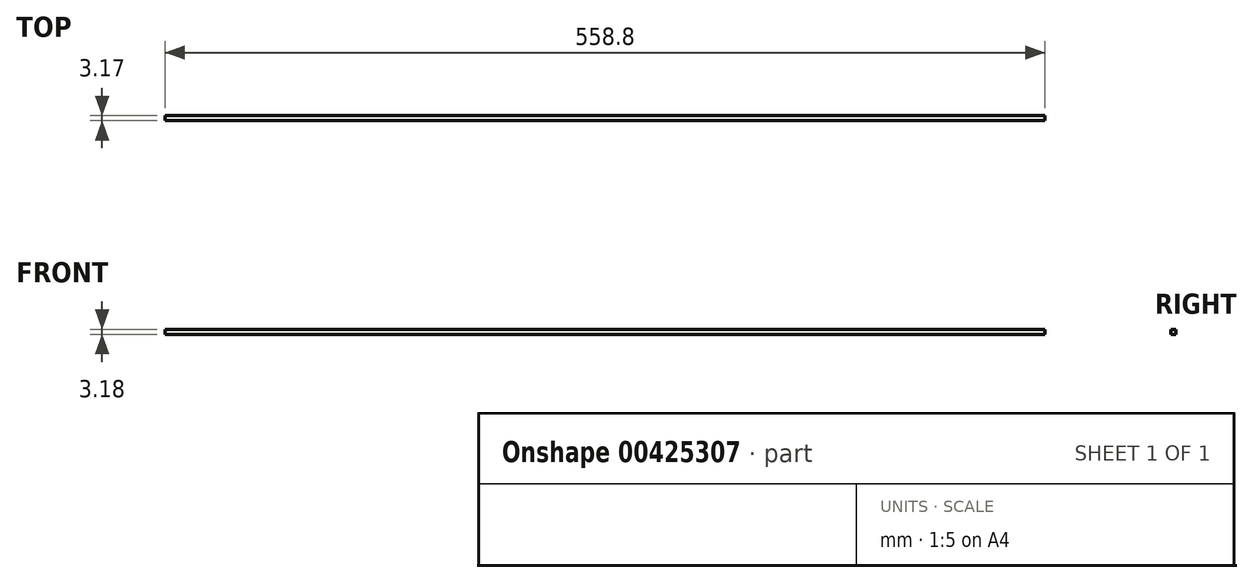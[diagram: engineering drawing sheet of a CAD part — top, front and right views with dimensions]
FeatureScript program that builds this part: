
annotation { "Feature Type Name" : "Feature", "Feature Type Description" : "" }
export const myFeature = defineFeature(function(context is Context, id is Id, definition is map)
    precondition{}
    {
        {
            var Q0;
            Q0=qCreatedBy(makeId("Front.planeOp"),FACE);
            var sketch = newSketch(context, id + "F0", { "sketchPlane" : qUnion([Q0])});
            skLineSegment(sketch, "E0.bottom", {"start": v(-289.72, -37.1) * mm, "end": v(269.08, -37.1) * mm});
            skLineSegment(sketch, "E0.top", {"start": v(-289.72, -40.27) * mm, "end": v(269.08, -40.27) * mm});
            skLineSegment(sketch, "E0.left", {"start": v(-289.72, -37.1) * mm, "end": v(-289.72, -40.27) * mm});
            skLineSegment(sketch, "E0.right", {"start": v(269.08, -37.1) * mm, "end": v(269.08, -40.27) * mm});
            skSolve(sketch);
        }
        {
            var Q0;
            Q0=makeQuery(id+"F0.imprint","IMPRINT",FACE,{"disambiguationData":[TD([[makeQuery(id+"F0.imprint","IMPRINT",EDGE,{"derivedFrom":sQuery(id+"F0.wireOp",EDGE,"E0.bottom")}),-1.0]])]});
            extrude(context, id + "F1", {"entities" : qUnion([Q0]), "depth" : 3.17 * mm});
        }
    });
